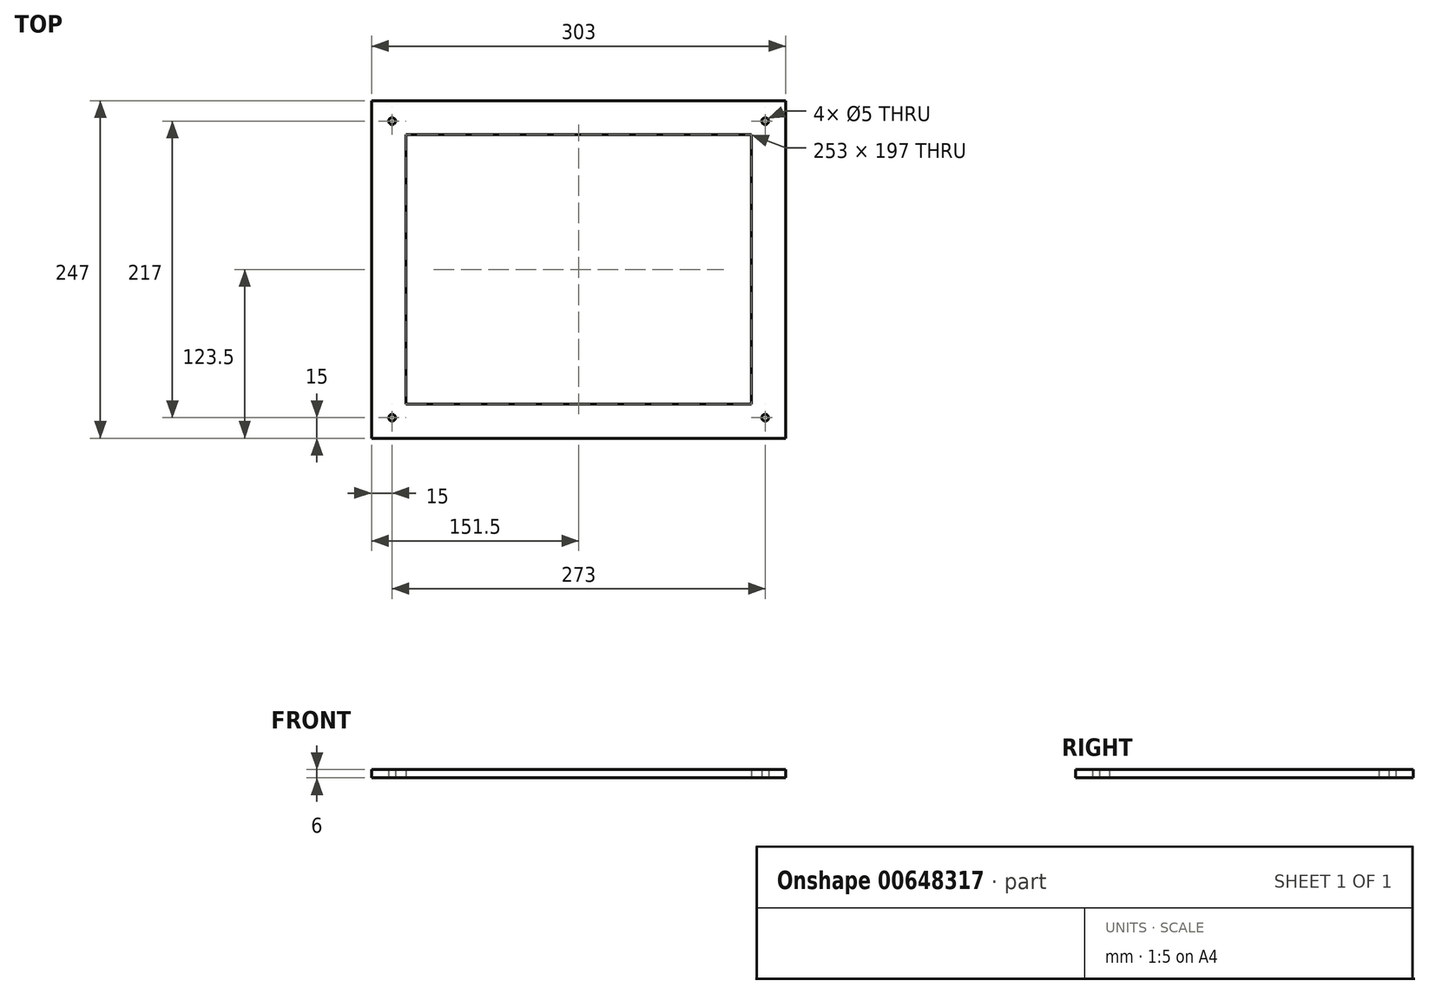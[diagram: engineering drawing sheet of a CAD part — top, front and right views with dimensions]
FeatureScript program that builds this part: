
annotation { "Feature Type Name" : "Feature", "Feature Type Description" : "" }
export const myFeature = defineFeature(function(context is Context, id is Id, definition is map)
    precondition{}
    {
        {
            var Q0;
            Q0=qCreatedBy(makeId("Top.planeOp"),FACE);
            var sketch = newSketch(context, id + "F0", { "sketchPlane" : qUnion([Q0])});
            skLineSegment(sketch, "E0.bottom", {"start": v(-136.5, 108.5) * mm, "end": v(136.5, 108.5) * mm, "construction": true});
            skLineSegment(sketch, "E0.top", {"start": v(-136.5, -108.5) * mm, "end": v(136.5, -108.5) * mm, "construction": true});
            skLineSegment(sketch, "E0.left", {"start": v(-136.5, 108.5) * mm, "end": v(-136.5, -108.5) * mm, "construction": true});
            skLineSegment(sketch, "E0.right", {"start": v(136.5, 108.5) * mm, "end": v(136.5, -108.5) * mm, "construction": true});
            skCircle(sketch, "E1", {"center": v(-136.5, 108.5) * mm, "radius": 2.5 * mm});
            skCircle(sketch, "E2", {"center": v(136.5, 108.5) * mm, "radius": 2.5 * mm});
            skCircle(sketch, "E3", {"center": v(136.5, -108.5) * mm, "radius": 2.5 * mm});
            skCircle(sketch, "E4", {"center": v(-136.5, -108.5) * mm, "radius": 2.5 * mm});
            skLineSegment(sketch, "E5.0", {"start": v(-151.5, 123.5) * mm, "end": v(151.5, 123.5) * mm});
            skLineSegment(sketch, "E5.1", {"start": v(-151.5, 123.5) * mm, "end": v(-151.5, -123.5) * mm});
            skLineSegment(sketch, "E5.2", {"start": v(-151.5, -123.5) * mm, "end": v(151.5, -123.5) * mm});
            skLineSegment(sketch, "E5.3", {"start": v(151.5, 123.5) * mm, "end": v(151.5, -123.5) * mm});
            skLineSegment(sketch, "E6.0", {"start": v(-126.5, 98.5) * mm, "end": v(126.5, 98.5) * mm});
            skLineSegment(sketch, "E6.1", {"start": v(-126.5, 98.5) * mm, "end": v(-126.5, -98.5) * mm});
            skLineSegment(sketch, "E6.2", {"start": v(-126.5, -98.5) * mm, "end": v(126.5, -98.5) * mm});
            skLineSegment(sketch, "E6.3", {"start": v(126.5, 98.5) * mm, "end": v(126.5, -98.5) * mm});
            skSolve(sketch);
        }
        {
            var Q0;
            Q0 = qSketchRegion(id + "F0", true);
            extrude(context, id + "F1", {"entities" : qUnion([Q0]), "depth" : 6 * mm, "offsetDistance" : 25 * mm});
        }
    });
